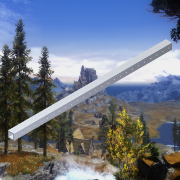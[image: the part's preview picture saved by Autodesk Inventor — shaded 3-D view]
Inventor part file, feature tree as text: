
AUTODESK INVENTOR PART (.ipt)
format: ipt  version: 2015 SP1 (Build 190203100, 203)  size: 1,181,696 bytes
history: native  units: in
note: dims shown in document units (in); Inventor stores cm internally (conversion verified against a paired STEP export)
features: pattern_circular x1, other x1, plane x1, extrude x1, imported_body x1, sketch x1
ambient origin geometry x8: Origin, YZ Plane, XZ Plane, XY Plane, X Axis, Y Axis, Z Axis, Center Point
bodies: Body1 (feature_tree)
feature tree (6):
  pattern_circular  "CirPattern2"
  other  "VersaFrame 1 x 1 x 0.100 Pre-Drilled Tube Stock (59 length)(217-4104)1"
  plane  "Work Plane1"
  extrude  "Extrusion1"  Depth=26.0in TaperAngle=0.0deg
  imported_body  "Base1"
  sketch  "Sketch1"  dims[d0=26.0in d1=3936.9685in d2=0.0in]
